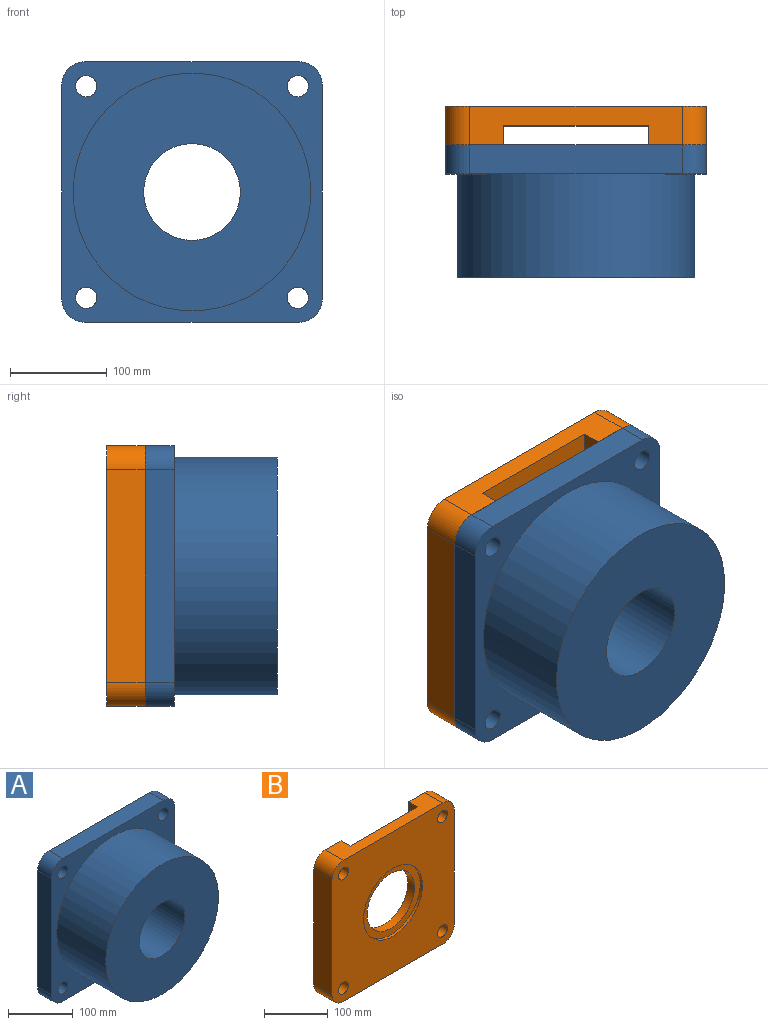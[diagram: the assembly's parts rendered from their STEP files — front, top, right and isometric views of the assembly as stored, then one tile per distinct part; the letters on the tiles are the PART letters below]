
ASSEMBLY  parts=2 mates=1
PART A: 17 faces, bbox 270x137x270 mm
  f0: plane 220x30mm, normal (1,0,0), area 6600mm2, adj f1,f7,f8,f9
  f1: cylinder r=25mm len=30mm, axis (0,1,0), area 1178.1mm2, adj f0,f2,f8,f9
  f2: plane 220x30mm, normal (0,0,1), area 6600mm2, adj f1,f3,f8,f9
  f3: cylinder r=25mm len=30mm, axis (0,1,0), area 1178.1mm2, adj f2,f4,f8,f9
  f4: plane 220x30mm, normal (-1,0,0), area 6600mm2, adj f3,f5,f8,f9
  f5: cylinder r=25mm len=30mm, axis (0,1,0), area 1178.1mm2, adj f4,f6,f8,f9
  f6: plane 220x30mm, normal (0,0,-1), area 6600mm2, adj f5,f7,f8,f9
  f7: cylinder r=25mm len=30mm, axis (0,1,0), area 1178.1mm2, adj f0,f6,f8,f9
  f8: plane 270x270mm, normal (0,-1,0), area 23313.8mm2, adj f0,f1,f2,f3,f4,f5,f6,f7
  f9: plane 270x270mm, normal (0,1,0), area 62989mm2, adj f0,f1,f2,f3,f4,f5,f6,f7
  f10: cylinder r=50mm len=137mm, axis (0,1,0), area 43039.8mm2, adj f9,f12
  f11: cylinder r=123mm len=246mm, axis (0,1,0), area 82693mm2, adj f8,f12
  f12: plane 246x246mm, normal (0,-1,0), area 39675.2mm2, adj f10,f11
  f13: cylinder r=11mm len=30mm, axis (0,-1,0), area 2073.5mm2, adj f8,f9
  f14: cylinder r=11mm len=30mm, axis (0,-1,0), area 2073.5mm2, adj f8,f9
  f15: cylinder r=11mm len=30mm, axis (0,-1,0), area 2073.5mm2, adj f8,f9
  f16: cylinder r=11mm len=30mm, axis (0,-1,0), area 2073.5mm2, adj f8,f9
PART B: 21 faces, bbox 270x40x270 mm
  f0: cylinder r=52.5mm len=105mm, axis (0,1,0), area 4948mm2, adj f18,f20
  f1: plane 270x60mm, normal (0,1,0), area 15171.5mm2, adj f2,f3,f4,f5,f9,f12,f15,f16
  f2: plane 220x40mm, normal (0,0,-1), area 5800mm2, adj f1,f8,f9,f10,f11,f16,f17,f18
  f3: plane 220x40mm, normal (1,0,0), area 8800mm2, adj f1,f4,f9,f10
  f4: cylinder r=25mm len=40mm, axis (0,1,0), area 1570.8mm2, adj f1,f3,f5,f10
  f5: plane 220x40mm, normal (0,0,1), area 5800mm2, adj f1,f4,f6,f10,f11,f16,f17,f18
  f6: cylinder r=25mm len=40mm, axis (0,1,0), area 1570.8mm2, adj f5,f7,f10,f11
  f7: plane 220x40mm, normal (-1,0,0), area 8800mm2, adj f6,f8,f10,f11
  f8: cylinder r=25mm len=40mm, axis (0,1,0), area 1570.8mm2, adj f2,f7,f10,f11
  f9: cylinder r=25mm len=40mm, axis (0,1,0), area 1570.8mm2, adj f1,f2,f3,f10
  f10: plane 270x270mm, normal (0,-1,0), area 57569.7mm2, adj f2,f3,f4,f5,f6,f7,f8,f9
  f11: plane 270x60mm, normal (0,1,0), area 15171.5mm2, adj f2,f5,f6,f7,f8,f13,f14,f17
  f12: cylinder r=11mm len=40mm, axis (0,1,0), area 2764.6mm2, adj f1,f10
  f13: cylinder r=11mm len=40mm, axis (0,1,0), area 2764.6mm2, adj f10,f11
  f14: cylinder r=11mm len=40mm, axis (0,1,0), area 2764.6mm2, adj f10,f11
  f15: cylinder r=11mm len=40mm, axis (0,1,0), area 2764.6mm2, adj f1,f10
  f16: plane 270x20mm, normal (-1,0,0), area 5400mm2, adj f1,f2,f5,f18
  f17: plane 270x20mm, normal (1,0,0), area 5400mm2, adj f2,f5,f11,f18
  f18: plane 270x150mm, normal (0,1,0), area 31841mm2, adj f0,f2,f5,f16,f17
  f19: cylinder r=65mm len=130mm, axis (0,-1,0), area 2042mm2, adj f10,f20
  f20: plane 130x130mm, normal (0,-1,0), area 4614.2mm2, adj f0,f19
PLACE A at identity fixed
PLACE B rot(axis=(1,0,0),180deg) t=(0,0,0)mm
MATE planar B.f11 <-> A.f11  axis (0,-1,0) through (-104.34,0,0)mm
